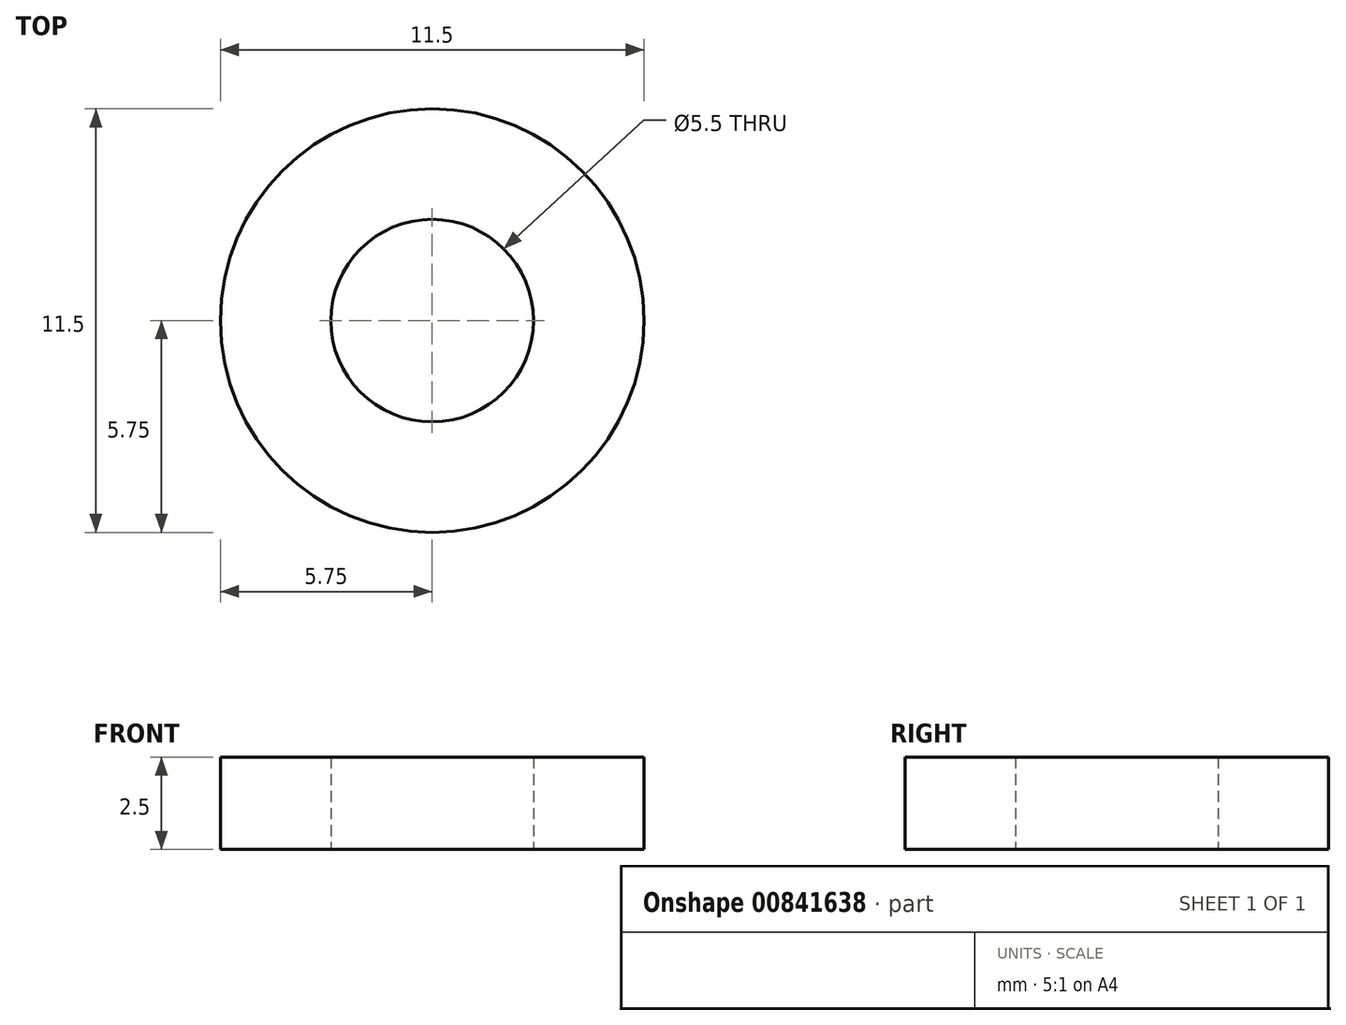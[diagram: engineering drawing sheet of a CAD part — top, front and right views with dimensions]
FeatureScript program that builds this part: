
annotation { "Feature Type Name" : "Feature", "Feature Type Description" : "" }
export const myFeature = defineFeature(function(context is Context, id is Id, definition is map)
    precondition{}
    {
        {
            var Q0;
            Q0=qCreatedBy(makeId("Top.planeOp"),FACE);
            var sketch = newSketch(context, id + "F0", { "sketchPlane" : qUnion([Q0])});
            skCircle(sketch, "E0", {"center": v(0, 0) * mm, "radius": 5.75 * mm});
            skCircle(sketch, "E1", {"center": v(0, 0) * mm, "radius": 2.75 * mm});
            skSolve(sketch);
        }
        {
            var Q0;
            Q0=makeQuery(id+"F0.imprint","IMPRINT",FACE,{"disambiguationData":[TD([[makeQuery(id+"F0.imprint","IMPRINT",EDGE,{"derivedFrom":sQuery(id+"F0.wireOp",EDGE,"E0")}),1.0]])]});
            extrude(context, id + "F1", {"entities" : qUnion([Q0]), "depth" : 2.5 * mm, "offsetDistance" : 25 * mm});
        }
    });
